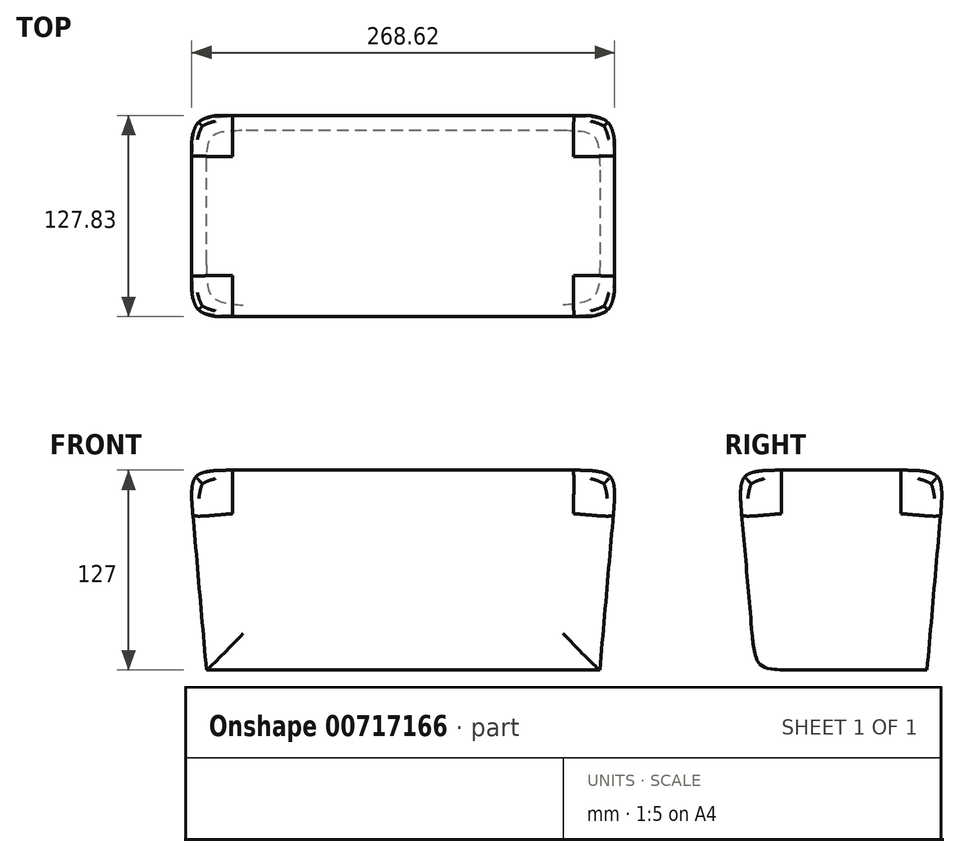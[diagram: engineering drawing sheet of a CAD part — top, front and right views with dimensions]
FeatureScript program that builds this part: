
annotation { "Feature Type Name" : "Feature", "Feature Type Description" : "" }
export const myFeature = defineFeature(function(context is Context, id is Id, definition is map)
    precondition{}
    {
        {
            var Q0;
            Q0=qCreatedBy(makeId("Top.planeOp"),FACE);
            var sketch = newSketch(context, id + "F0", { "sketchPlane" : qUnion([Q0])});
            skLineSegment(sketch, "E0.bottom", {"start": v(-127.75, 58.54) * mm, "end": v(122.07, 58.54) * mm});
            skLineSegment(sketch, "E0.top", {"start": v(-127.75, -50.5) * mm, "end": v(122.07, -50.5) * mm});
            skLineSegment(sketch, "E0.left", {"start": v(-127.75, 58.54) * mm, "end": v(-127.75, -50.5) * mm});
            skLineSegment(sketch, "E0.right", {"start": v(122.07, 58.54) * mm, "end": v(122.07, -50.5) * mm});
            skSolve(sketch);
        }
        {
            var Q0;
            Q0 = qSketchRegion(id + "F0", true);
            extrude(context, id + "F1", {"entities" : qUnion([Q0]), "depth" : 127 * mm, "offsetDistance" : 25.4 * mm, "hasDraft" : true, "draftAngle" : 5 * degree});
        }
        {
            var Q0;
            Q0=makeQuery(id+"F1.opExtrude","CAP_EDGE",EDGE,{"disambiguationData":[OSD([sQuery(id+"F0.wireOp",EDGE,"E0.right")])],"isStart":false});
            var Q1;
            Q1=makeQuery(id+"F1.opExtrude","CAP_EDGE",EDGE,{"disambiguationData":[OSD([sQuery(id+"F0.wireOp",EDGE,"E0.top")])],"isStart":false});
            var Q2;
            Q2=makeQuery(id+"F1.opExtrude","CAP_EDGE",EDGE,{"disambiguationData":[OSD([sQuery(id+"F0.wireOp",EDGE,"E0.left")])],"isStart":false});
            var Q3;
            Q3=makeQuery(id+"F1.opExtrude","CAP_EDGE",EDGE,{"disambiguationData":[OSD([sQuery(id+"F0.wireOp",EDGE,"E0.bottom")])],"isStart":false});
            var Q4;
            Q4=makeQuery(id+"F1.opExtrude","SWEPT_EDGE",EDGE,{"disambiguationData":[OSD([sQuery(id+"F0.wireOp",EDGE,"E0.top"),sQuery(id+"F0.wireOp",EDGE,"E0.right")])]});
            var Q5;
            Q5=makeQuery(id+"F1.opExtrude","SWEPT_EDGE",EDGE,{"disambiguationData":[OSD([sQuery(id+"F0.wireOp",EDGE,"E0.top"),sQuery(id+"F0.wireOp",EDGE,"E0.left")])]});
            var Q6;
            Q6=makeQuery(id+"F1.opExtrude","SWEPT_EDGE",EDGE,{"disambiguationData":[OSD([sQuery(id+"F0.wireOp",EDGE,"E0.bottom"),sQuery(id+"F0.wireOp",EDGE,"E0.left")])]});
            var Q7;
            Q7=makeQuery(id+"F1.opExtrude","SWEPT_EDGE",EDGE,{"disambiguationData":[OSD([sQuery(id+"F0.wireOp",EDGE,"E0.bottom"),sQuery(id+"F0.wireOp",EDGE,"E0.right")])]});
            var Q8;
            Q8=makeQuery(id+"F1.opExtrude","CAP_EDGE",EDGE,{"disambiguationData":[OSD([sQuery(id+"F0.wireOp",EDGE,"E0.top")])],"isStart":true});
            fillet(context, id + "F2", {"entities" : qUnion([Q0, Q1, Q2, Q3, Q4, Q5, Q6, Q7, Q8]), "radius" : 25.4 * mm, "tangentPropagation" : true, "rho" : .7, "crossSection" : FilletCrossSection.CONIC, "allowEdgeOverflow" : false});
        }
    });
